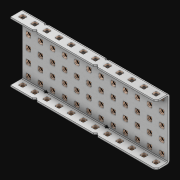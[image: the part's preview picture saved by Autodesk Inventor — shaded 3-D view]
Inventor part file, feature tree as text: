
AUTODESK INVENTOR PART (.ipt)
format: ipt  version: 2021 (Build 250183000, 183)  size: 3,128,320 bytes
history: native  units: in
note: dims shown in document units (in); Inventor stores cm internally (conversion verified against a paired STEP export)
features: extrude x85, other x84, sketch x4, thicken_offset x3, pattern_linear x3, imported_body x1
ambient origin geometry x8: Origin, YZ Plane, XZ Plane, XY Plane, X Axis, Y Axis, Z Axis, Center Point
bodies: Solid1 (feature_tree)
feature tree (180):
  thicken_offset  "Thicken1"
  thicken_offset  "Thicken2"
  thicken_offset  "Thicken3"
  pattern_linear  "Rectangular Pattern1"  Spacing1=0.001in  [1 undecoded]
  pattern_linear  "Rectangular Pattern2"  Spacing1=0.001in  [1 undecoded]
  pattern_linear  "Rectangular Pattern3"  Spacing1=0.182in  [1 undecoded]
  extrude  "Extrusion1"  Depth=0.063in TaperAngle=0.0deg
  sketch  "Sketch1"  dims[d0=0.001in]
  other  "Srf1"
  sketch  "Sketch2"  dims[d1=0.001in]
  other  "Srf2"
  sketch  "Sketch3"  dims[d2=0.001in]
  other  "Srf3"
  other  "Srf4"
  other  "Srf5"
  other  "Srf6"
  other  "Srf7"
  other  "Srf8"
  other  "Srf9"
  other  "Srf10"
  other  "Srf11"
  other  "Srf12"
  other  "Srf13"
  other  "Srf14"
  other  "Srf38"
  other  "Srf39"
  other  "Srf40"
  other  "Srf41"
  other  "Srf42"
  other  "Srf43"
  other  "Srf44"
  other  "Srf45"
  other  "Srf46"
  other  "Srf47"
  other  "Srf48"
  other  "Srf72"
  other  "Srf73"
  other  "Srf74"
  other  "Srf75"
  other  "Srf76"
  other  "Srf77"
  other  "Srf78"
  other  "Srf79"
  other  "Srf80"
  other  "Srf81"
  other  "Srf82"
  other  "Srf106"
  other  "Srf107"
  other  "Srf108"
  other  "Srf109"
  other  "Srf110"
  other  "Srf111"
  other  "Srf112"
  other  "Srf113"
  other  "Srf114"
  other  "Srf115"
  other  "Srf116"
  other  "Srf117"
  other  "Srf141"
  other  "Srf142"
  other  "Srf143"
  other  "Srf144"
  other  "Srf145"
  other  "Srf146"
  other  "Srf147"
  other  "Srf148"
  other  "Srf149"
  other  "Srf150"
  other  "Srf151"
  other  "Srf152"
  other  "Srf176"
  other  "Srf177"
  other  "Srf178"
  other  "Srf179"
  other  "Srf180"
  other  "Srf181"
  other  "Srf182"
  other  "Srf183"
  other  "Srf184"
  other  "Srf185"
  other  "Srf186"
  other  "Srf187"
  other  "Srf211"
  other  "Srf212"
  other  "Srf213"
  other  "Srf214"
  other  "Srf215"
  other  "Srf216"
  other  "Srf217"
  other  "Srf218"
  other  "Srf219"
  other  "Srf220"
  other  "Srf221"
  other  "Srf222"
  sketch  "Sketch4"  dims[d3=0.001in d4=0.001in d5=0.001in d6=0.182in d7=0.063in d8=0.0in d9=0.182in d10=0.063in d11=0.0in d12=0.182in d13=0.063in d14=0.0in d17=0.5in d18=4.7244in d20=0.5in d21=4.7244in d23=0.5in d24=1.9685in d26=0.5in d27=11.5in d28=0.0in]
  imported_body  "Imported1"
  extrude  "ExtrusionSrf1"  Depth=0.063in
  extrude  "ExtrusionSrf2"  Depth=0.063in TaperAngle=0.0deg
  extrude  "ExtrusionSrf3"  Depth=0.063in
  extrude  "ExtrusionSrf4"  Depth=0.063in TaperAngle=0.0deg
  extrude  "ExtrusionSrf5"  Depth=0.063in
  extrude  "ExtrusionSrf6"  Depth=0.063in
  extrude  "ExtrusionSrf7"  Depth=0.063in
  extrude  "ExtrusionSrf8"  Depth=0.063in
  extrude  "ExtrusionSrf9"  Depth=0.063in
  extrude  "ExtrusionSrf10"  Depth=0.063in
  extrude  "ExtrusionSrf11"  Depth=0.063in
  extrude  "ExtrusionSrf12"  TaperAngle=0.0deg  [1 undecoded]
  extrude  "ExtrusionSrf13"  [1 undecoded]
  extrude  "ExtrusionSrf14"  [1 undecoded]
  extrude  "ExtrusionSrf38"  [1 undecoded]
  extrude  "ExtrusionSrf39"  [1 undecoded]
  extrude  "ExtrusionSrf40"  [1 undecoded]
  extrude  "ExtrusionSrf41"  [1 undecoded]
  extrude  "ExtrusionSrf42"  [1 undecoded]
  extrude  "ExtrusionSrf43"  [1 undecoded]
  extrude  "ExtrusionSrf44"  [1 undecoded]
  extrude  "ExtrusionSrf45"  [1 undecoded]
  extrude  "ExtrusionSrf46"  [1 undecoded]
  extrude  "ExtrusionSrf47"  [1 undecoded]
  extrude  "ExtrusionSrf48"  [1 undecoded]
  extrude  "ExtrusionSrf72"  [1 undecoded]
  extrude  "ExtrusionSrf73"  [1 undecoded]
  extrude  "ExtrusionSrf74"  [1 undecoded]
  extrude  "ExtrusionSrf75"  [1 undecoded]
  extrude  "ExtrusionSrf76"  [1 undecoded]
  extrude  "ExtrusionSrf77"  [1 undecoded]
  extrude  "ExtrusionSrf78"  [1 undecoded]
  extrude  "ExtrusionSrf79"  [1 undecoded]
  extrude  "ExtrusionSrf80"  [1 undecoded]
  extrude  "ExtrusionSrf81"  [1 undecoded]
  extrude  "ExtrusionSrf82"  [1 undecoded]
  extrude  "ExtrusionSrf106"  [1 undecoded]
  extrude  "ExtrusionSrf107"  [1 undecoded]
  extrude  "ExtrusionSrf108"  [1 undecoded]
  extrude  "ExtrusionSrf109"  [1 undecoded]
  extrude  "ExtrusionSrf110"  [1 undecoded]
  extrude  "ExtrusionSrf111"  [1 undecoded]
  extrude  "ExtrusionSrf112"  [1 undecoded]
  extrude  "ExtrusionSrf113"  [1 undecoded]
  extrude  "ExtrusionSrf114"  [1 undecoded]
  extrude  "ExtrusionSrf115"  [1 undecoded]
  extrude  "ExtrusionSrf116"  [1 undecoded]
  extrude  "ExtrusionSrf117"  [1 undecoded]
  extrude  "ExtrusionSrf141"  [1 undecoded]
  extrude  "ExtrusionSrf142"  [1 undecoded]
  extrude  "ExtrusionSrf143"  [1 undecoded]
  extrude  "ExtrusionSrf144"  [1 undecoded]
  extrude  "ExtrusionSrf145"  [1 undecoded]
  extrude  "ExtrusionSrf146"  [1 undecoded]
  extrude  "ExtrusionSrf147"  [1 undecoded]
  extrude  "ExtrusionSrf148"  [1 undecoded]
  extrude  "ExtrusionSrf149"  [1 undecoded]
  extrude  "ExtrusionSrf150"  [1 undecoded]
  extrude  "ExtrusionSrf151"  [1 undecoded]
  extrude  "ExtrusionSrf152"  [1 undecoded]
  extrude  "ExtrusionSrf176"  [1 undecoded]
  extrude  "ExtrusionSrf177"  [1 undecoded]
  extrude  "ExtrusionSrf178"  [1 undecoded]
  extrude  "ExtrusionSrf179"  [1 undecoded]
  extrude  "ExtrusionSrf180"  [1 undecoded]
  extrude  "ExtrusionSrf181"  [1 undecoded]
  extrude  "ExtrusionSrf182"  [1 undecoded]
  extrude  "ExtrusionSrf183"  [1 undecoded]
  extrude  "ExtrusionSrf184"  [1 undecoded]
  extrude  "ExtrusionSrf185"  [1 undecoded]
  extrude  "ExtrusionSrf186"  [1 undecoded]
  extrude  "ExtrusionSrf187"  [1 undecoded]
  extrude  "ExtrusionSrf211"  [1 undecoded]
  extrude  "ExtrusionSrf212"  [1 undecoded]
  extrude  "ExtrusionSrf213"  [1 undecoded]
  extrude  "ExtrusionSrf214"  [1 undecoded]
  extrude  "ExtrusionSrf215"  [1 undecoded]
  extrude  "ExtrusionSrf216"  [1 undecoded]
  extrude  "ExtrusionSrf217"  [1 undecoded]
  extrude  "ExtrusionSrf218"  [1 undecoded]
  extrude  "ExtrusionSrf219"  [1 undecoded]
  extrude  "ExtrusionSrf220"  [1 undecoded]
  extrude  "ExtrusionSrf221"  [1 undecoded]
  extrude  "ExtrusionSrf222"  [1 undecoded]
note: 76 required parameter values undecoded (feature->parameter linkage not recoverable at this tier; creation-order binding heuristic only, values carry confidence <= 0.55)
